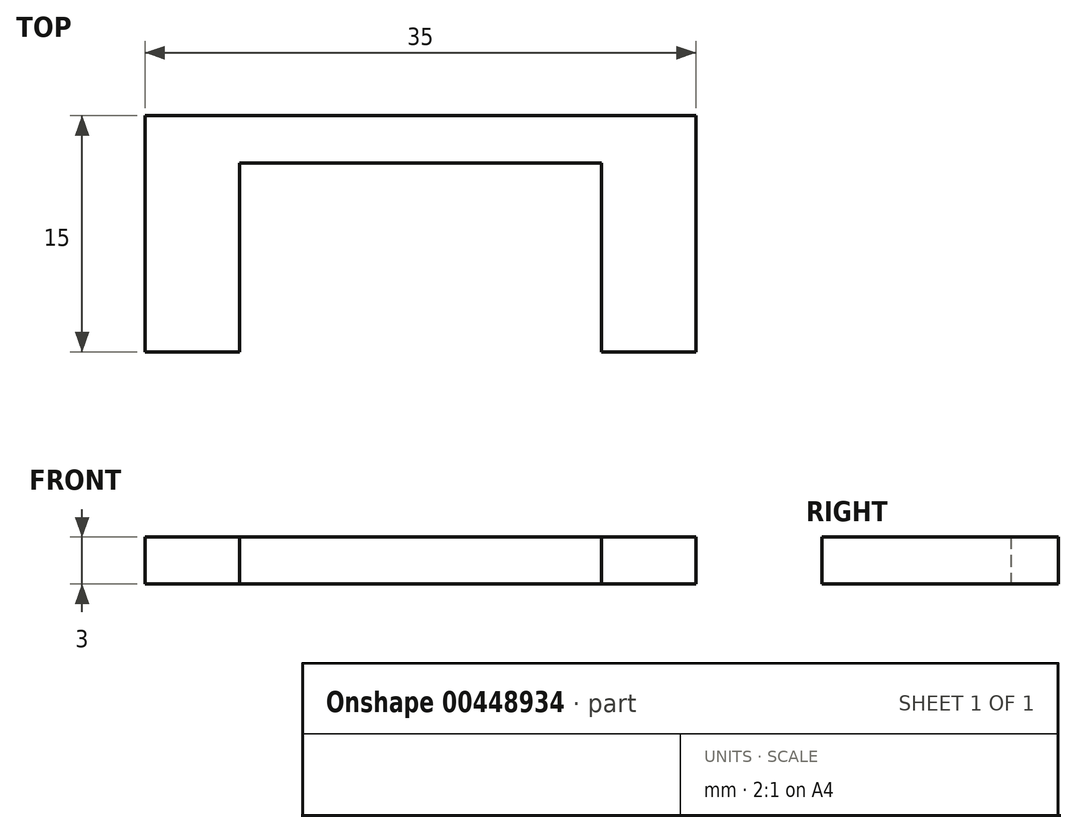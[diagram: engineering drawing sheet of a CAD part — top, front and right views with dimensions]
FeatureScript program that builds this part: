
annotation { "Feature Type Name" : "Feature", "Feature Type Description" : "" }
export const myFeature = defineFeature(function(context is Context, id is Id, definition is map)
    precondition{}
    {
        {
            var Q0;
            Q0=qCreatedBy(makeId("Top.planeOp"),FACE);
            var sketch = newSketch(context, id + "F0", { "sketchPlane" : qUnion([Q0])});
            skLineSegment(sketch, "E0", {"start": v(-29, 22.76) * mm, "end": v(-29, 7.76) * mm});
            skLineSegment(sketch, "E1", {"start": v(-29, 22.76) * mm, "end": v(6, 22.76) * mm});
            skLineSegment(sketch, "E2", {"start": v(6, 22.76) * mm, "end": v(6, 7.76) * mm});
            skLineSegment(sketch, "E3", {"start": v(6, 7.76) * mm, "end": v(0, 7.76) * mm});
            skLineSegment(sketch, "E4", {"start": v(0, 7.76) * mm, "end": v(0, 19.76) * mm});
            skLineSegment(sketch, "E5", {"start": v(0, 19.76) * mm, "end": v(-23, 19.76) * mm});
            skLineSegment(sketch, "E6", {"start": v(-23, 19.76) * mm, "end": v(-23, 7.76) * mm});
            skLineSegment(sketch, "E7", {"start": v(-23, 7.76) * mm, "end": v(-29, 7.76) * mm});
            skSolve(sketch);
        }
        {
            var Q0;
            Q0=makeQuery(id+"F0.imprint","IMPRINT",FACE,{"disambiguationData":[TD([[makeQuery(id+"F0.imprint","IMPRINT",EDGE,{"derivedFrom":sQuery(id+"F0.wireOp",EDGE,"E0")}),1.0]])]});
            extrude(context, id + "F1", {"entities" : qUnion([Q0]), "depth" : 3 * mm});
        }
    });
